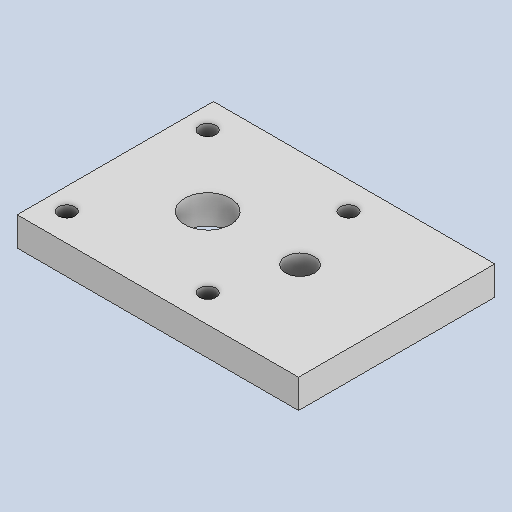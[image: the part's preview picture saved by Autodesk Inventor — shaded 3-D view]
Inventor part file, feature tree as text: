
AUTODESK INVENTOR PART (.ipt)
format: ipt  version: 2025.1 (Build 291241020, 241B)  size: 147,968 bytes
history: native  units: in
note: dims shown in document units (in); Inventor stores cm internally (conversion verified against a paired STEP export)
features: hole x4, sketch x3, extrude x1
ambient origin geometry x8: Origin, YZ Plane, XZ Plane, XY Plane, X Axis, Y Axis, Z Axis, Center Point
bodies: Solid1 (feature_tree)
feature tree (8):
  extrude  "Extrusion1"  Depth=1.7in
  sketch  "Sketch2"  dims[d2=0.25in d3=0.0in d4=0.2398in]
  hole  "Hole1"  [1 undecoded]
  hole  "Hole2"  [1 undecoded]
  hole  "Hole3"  [1 undecoded]
  hole  "Hole4"  [1 undecoded]
  sketch  "Sketch1"  dims[d0=2.4375in d1=1.7in]
  sketch  "Sketch3"  dims[d5=0.1898in d6=0.2398in d7=0.1898in d8=0.2398in d9=1.0273in d10=0.8375in d11=0.85in d12=0.2398in d13=1.0273in d14=0.85in d15=0.8in d16=0.142in d17=0.276in d18=0.375in d19=0.25in d20=0.5635in d21=0.432in d22=0.8108in d23=0.3976in d24=0.75in d25=0.375in d26=0.25in d27=0.5635in d28=0.432in d29=0.8108in d30=0.104in d31=0.276in d32=0.279in d33=0.25in d34=0.5635in d35=0.5in d36=0.8108in d37=0.45in d38=0.45in d39=0.125in d40=0.25in d41=0.75in d42=0.375in d43=0.25in d44=0.5635in d45=0.432in d46=0.8108in]
note: 4 required parameter values undecoded (feature->parameter linkage not recoverable at this tier; creation-order binding heuristic only, values carry confidence <= 0.55)
